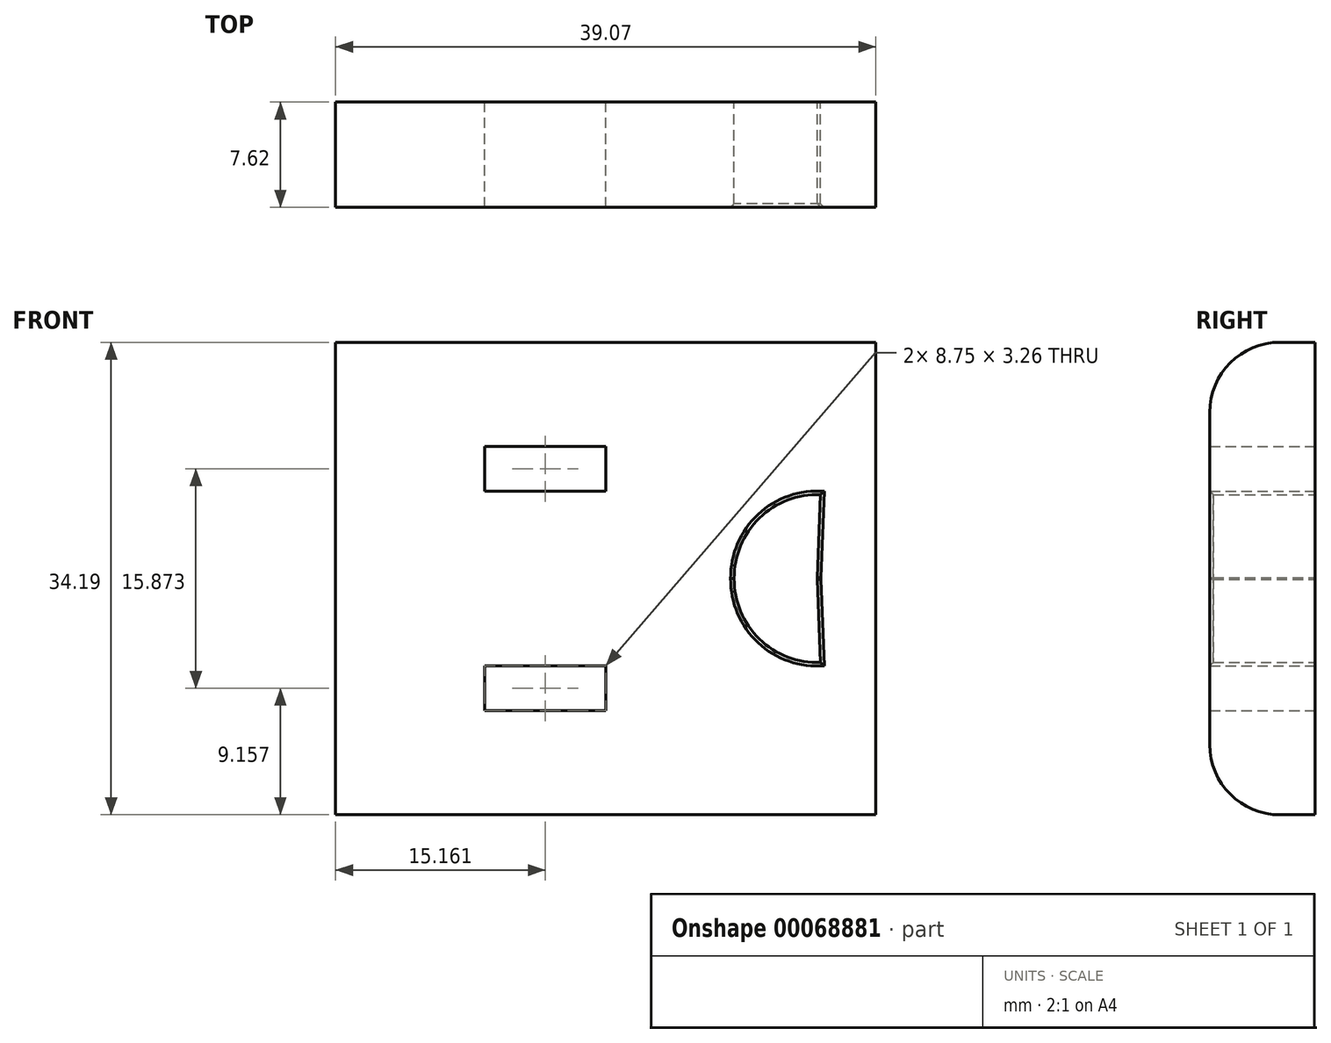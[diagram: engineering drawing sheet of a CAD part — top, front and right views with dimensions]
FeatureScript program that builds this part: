
annotation { "Feature Type Name" : "Feature", "Feature Type Description" : "" }
export const myFeature = defineFeature(function(context is Context, id is Id, definition is map)
    precondition{}
    {
        {
            var Q0;
            Q0=qCreatedBy(makeId("Front.planeOp"),FACE);
            var sketch = newSketch(context, id + "F0", { "sketchPlane" : qUnion([Q0])});
            skLineSegment(sketch, "E0.bottom", {"start": v(0, 0) * mm, "end": v(39.07, 0) * mm});
            skLineSegment(sketch, "E0.top", {"start": v(0, 34.19) * mm, "end": v(39.07, 34.19) * mm});
            skLineSegment(sketch, "E0.left", {"start": v(0, 0) * mm, "end": v(0, 34.19) * mm});
            skLineSegment(sketch, "E0.right", {"start": v(39.07, 0) * mm, "end": v(39.07, 34.19) * mm});
            skPoint(sketch, "E1.oppositeSnap0", {"position": v(19.54, 34.19) * mm});
            skLineSegment(sketch, "E1.bottom", {"start": v(10.79, 23.4) * mm, "end": v(19.54, 23.4) * mm});
            skLineSegment(sketch, "E1.top", {"start": v(10.79, 26.66) * mm, "end": v(19.54, 26.66) * mm});
            skLineSegment(sketch, "E1.left", {"start": v(10.79, 23.4) * mm, "end": v(10.79, 26.66) * mm});
            skLineSegment(sketch, "E1.right", {"start": v(19.54, 23.4) * mm, "end": v(19.54, 26.66) * mm});
            skLineSegment(sketch, "E2", {"start": v(0, 17.1) * mm, "end": v(39.07, 17.1) * mm, "construction": true});
            skArc(sketch, "E3", {"start": v(35.08, 23.17) * mm, "mid": v(30.65, 21.47) * mm, "end": v(28.83, 17.1) * mm});
            skLineSegment(sketch, "E4", {"start": v(34.84, 17.16) * mm, "end": v(35.08, 23.17) * mm});
            skLineSegment(sketch, "E5.MirrorCS", {"start": v(10.79, 10.79) * mm, "end": v(19.54, 10.79) * mm});
            skLineSegment(sketch, "E6.MirrorCS", {"start": v(10.79, 10.79) * mm, "end": v(10.79, 7.53) * mm});
            skLineSegment(sketch, "E7.MirrorCS", {"start": v(10.79, 7.53) * mm, "end": v(19.54, 7.53) * mm});
            skLineSegment(sketch, "E8.MirrorCS", {"start": v(19.54, 10.79) * mm, "end": v(19.54, 7.53) * mm});
            skArc(sketch, "E9.MirrorCS", {"start": v(35.08, 11.02) * mm, "mid": v(30.65, 12.72) * mm, "end": v(28.83, 17.1) * mm});
            skLineSegment(sketch, "E10.MirrorCS", {"start": v(34.84, 17.03) * mm, "end": v(35.08, 11.02) * mm});
            skPoint(sketch, "E11.orphan", {"position": v(34.18, 23) * mm});
            skPoint(sketch, "E12.orphan", {"position": v(34.18, 11.18) * mm});
            skLineSegment(sketch, "E13", {"start": v(34.84, 17.03) * mm, "end": v(34.84, 17.16) * mm});
            skSolve(sketch);
        }
        {
            var Q0;
            Q0=makeQuery(id+"F0.imprint","IMPRINT",FACE,{"disambiguationData":[TD([[makeQuery(id+"F0.imprint","IMPRINT",EDGE,{"derivedFrom":sQuery(id+"F0.wireOp",EDGE,"E0.bottom")}),1.0]])]});
            extrude(context, id + "F1", {"entities" : qUnion([Q0]), "depth" : 7.62 * mm});
        }
        {
            var Q0;
            Q0=makeQuery(id+"F1.opExtrude","CAP_EDGE",EDGE,{"disambiguationData":[OSD([sQuery(id+"F0.wireOp",EDGE,"E0.top")])],"isStart":false});
            fillet(context, id + "F2", {"entities" : qUnion([Q0]), "radius" : 5.08 * mm, "tangentPropagation" : true, "allowEdgeOverflow" : false});
        }
        {
            var Q0;
            Q0=makeQuery(id+"F1.opExtrude","CAP_EDGE",EDGE,{"disambiguationData":[OSD([sQuery(id+"F0.wireOp",EDGE,"E0.bottom")])],"isStart":false});
            fillet(context, id + "F3", {"entities" : qUnion([Q0]), "radius" : 5.08 * mm, "tangentPropagation" : true, "allowEdgeOverflow" : false});
        }
        {
            var Q0;
            Q0=makeQuery(id+"F1.opExtrude","CAP_EDGE",EDGE,{"disambiguationData":[OSD([sQuery(id+"F0.wireOp",EDGE,"E9.MirrorCS")])],"isStart":false});
            var Q1;
            Q1=makeQuery(id+"F1.opExtrude","CAP_EDGE",EDGE,{"disambiguationData":[OSD([sQuery(id+"F0.wireOp",EDGE,"E3")])],"isStart":false});
            var Q2;
            Q2=makeQuery(id+"F1.opExtrude","CAP_EDGE",EDGE,{"disambiguationData":[OSD([sQuery(id+"F0.wireOp",EDGE,"E4")])],"isStart":false});
            var Q3;
            Q3=makeQuery(id+"F1.opExtrude","CAP_EDGE",EDGE,{"disambiguationData":[OSD([sQuery(id+"F0.wireOp",EDGE,"E10.MirrorCS")])],"isStart":false});
            chamfer(context, id + "F4", {"entities" : qUnion([Q0, Q1, Q2, Q3]), "width" : 0.25 * mm, "tangentPropagation" : true});
        }
    });
